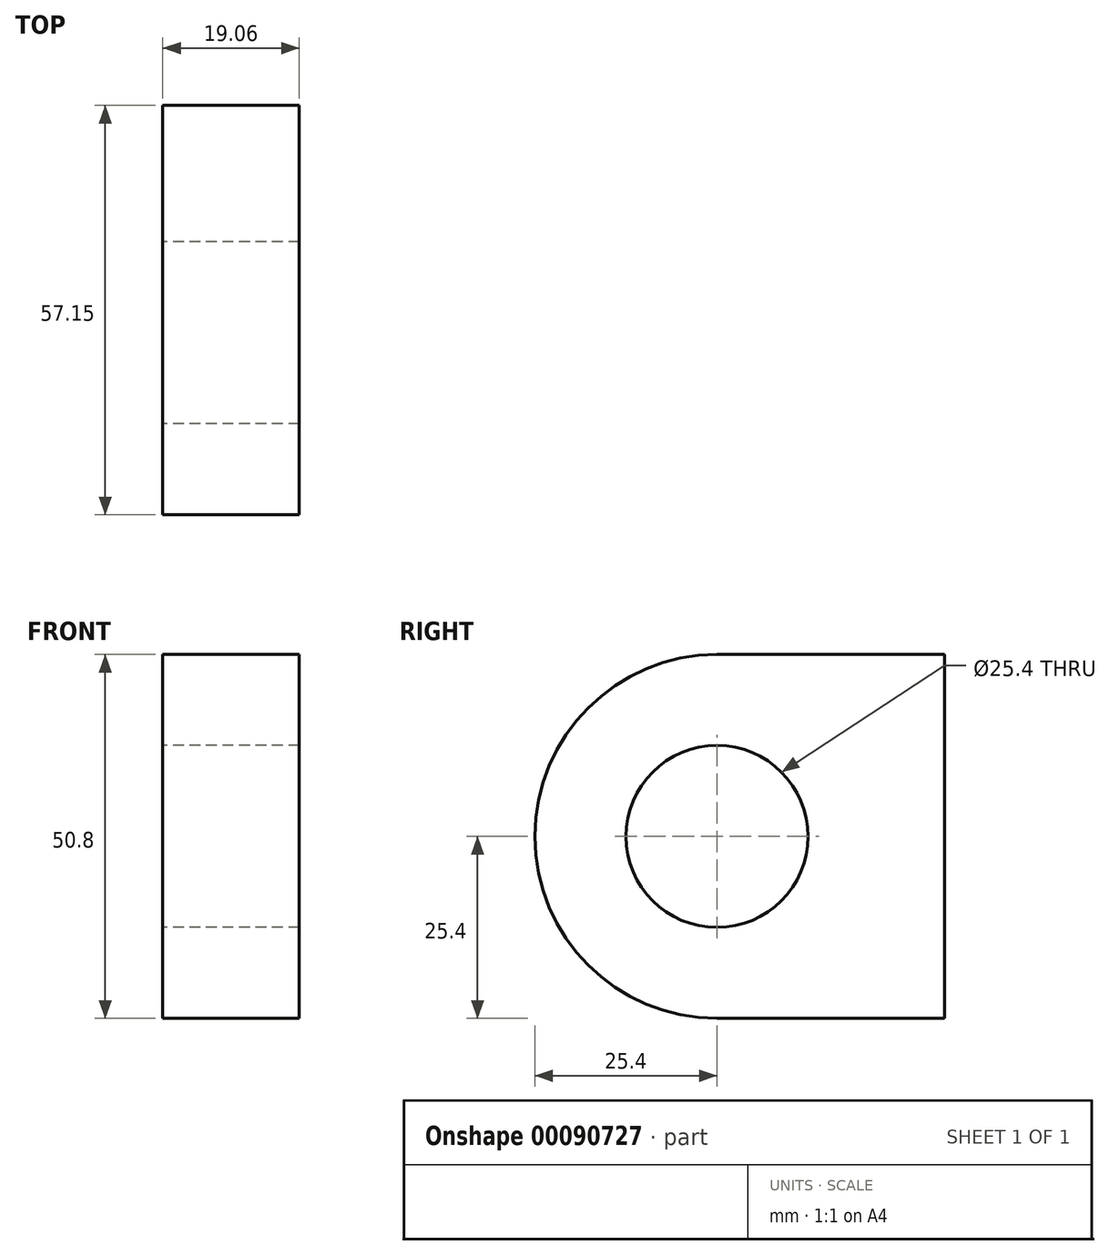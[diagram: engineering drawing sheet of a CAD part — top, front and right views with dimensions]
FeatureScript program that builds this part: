
annotation { "Feature Type Name" : "Feature", "Feature Type Description" : "" }
export const myFeature = defineFeature(function(context is Context, id is Id, definition is map)
    precondition{}
    {
        {
            var Q0;
            Q0=qCreatedBy(makeId("Right.planeOp"),FACE);
            var sketch = newSketch(context, id + "F0", { "sketchPlane" : qUnion([Q0])});
            skCircle(sketch, "E0", {"center": v(0, 0) * mm, "radius": 12.7 * mm});
            skArc(sketch, "E1", {"start": v(0, 25.4) * mm, "mid": v(-25.4, 0) * mm, "end": v(0, -25.4) * mm});
            skLineSegment(sketch, "E2.bottom", {"start": v(0, 25.4) * mm, "end": v(31.75, 25.4) * mm});
            skLineSegment(sketch, "E2.top", {"start": v(0, -25.4) * mm, "end": v(31.75, -25.4) * mm});
            skLineSegment(sketch, "E2.right", {"start": v(31.75, 25.4) * mm, "end": v(31.75, -25.4) * mm});
            skSolve(sketch);
        }
        {
            var Q0;
            Q0=makeQuery(id+"F0.imprint","IMPRINT",FACE,{"disambiguationData":[TD([[makeQuery(id+"F0.imprint","IMPRINT",EDGE,{"derivedFrom":sQuery(id+"F0.wireOp",EDGE,"E0")}),-1.0]])]});
            extrude(context, id + "F1", {"entities" : qUnion([Q0]), "endBound" : BoundingType.SYMMETRIC, "depth" : 19.05 * mm});
        }
    });
